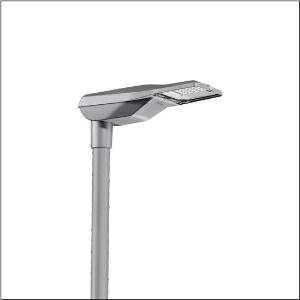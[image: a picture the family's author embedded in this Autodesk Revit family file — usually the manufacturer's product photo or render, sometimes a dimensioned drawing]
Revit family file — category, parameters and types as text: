
# Revit family: streetlight_sl_21_micro___st1_0a_5xe5d43a08db_2c1a
name_source: partatom
category: Lighting Fixtures
units: mm (PartAtom-declared; Revit-internal decimal feet)

## family parameters
Cut with Voids When Loaded = No
Host = Face
Light Source = No
Part Type = Normal
Room Calculation Point = No
Round Connector Dimension = Use Diameter
Shared = No

## types (1)
- --- (1 x LED, 5320 lm, 39.1 W, 4000K)
    Apparent Load = 39 VA
    CIE Flux Codes = 37 72 97 100 100
    Color Rendering = 70
    Color Temperature = 4000K
    Default Elevation = 1800 mm
    Description = Streetlight SL 21 micro, mast luminaire, primary light control with lens, of PMMA, primary optical cover: cover, of toughened safety glass, transparent, light distribution: ST1.0a, light emission: direct distribution, primary light characteristic: asymmetric, installation type: side-entry, post-top, LED, 3G 1.5mm², High Power LED, rated luminous flux: 5.320lm, luminous efficacy: 136lm/W, light colour: 740, colour temperature: 4000K, control: flexible luminous flux parameterisation, time-dependent luminous flux control, constant luminous flux control, overheat protection, mains connection: 230..240V, AC, 50/60Hz, connection cable pre-assembled, cable length: 6,5m, wiring characteristics: H07RN-F, start of lifetime: 39W, end of service life: 41W, reduction: 18W, luminaire housing, of diecast aluminium, powder-coated, Siteco® metallic grey (DB 702S), corrosivity category C5 mid according to DIN EN ISO 12944, please order mast flange separately, inclination adjustable: 0°, 5°, 10°, 15°, sealing non-destructively replaceable, multi-level sealing system, length: 528mm, width: 235mm, height: 110mm, mast flange for spigot size: 42mm (side-entry): 5XC10008XM4, 60/48mm (side-entry/post-top): 5XC10108XM2, 76/60mm (side-entry/post-top): 5XC10108XM1, protection rating (complete): IP66, insulation class (complete): insulation class II (safety insulation), certification: CE, ENEC, ENEC+, VDE, impact resistance: IK09, permissible operating ambient temperature for outdoor applications: -40..+50°C, standard-compliant lighting for roads and squares, packaging unit: 1 piece

Light Distribution: ST1.0a
    Height = 110 mm
    Lamp = 1 x LED
    Lamp Light Flux = 5320 lm
    Lamp Power = 39.1 W
    Lamp count = 1
    Length = 528 mm
    Luminous efficacy = 136 lm/W
    Manufacturer = Siteco
    ModVariant = No
    Model = 5XE5D43A08DB
    Number of Poles = 1
    OnlyDefault = Yes
    Power Factor = 1
    Product Name = Streetlight SL 21 micro | ST1.0a
    Product group = mast luminaire | pylon top
    ProductGroupID = 6100
    Protection Class = Protection class II
    Protection Degree = IP 66
    RLX_Detail_Level = 1
    RLX_Emergency_Light_Flux = 0 lm
    RLX_Emergency_Type = 0
    RLX_Emergency_Type_DB = No
    RlxData = <blob elided: 98429 chars, md5=3dc6498a>
    Socket = socket
    Standby Power = 0 W
    System Light Flux = 5320 lm
    System Power = 39 W
    Type Comments = factory setting: luminous flux: 100 % | Output Level: 100 % | 765 mA
    Type Image = l_1006881.jpg
    URL = http://relux.com
    VarID = @adj_105721
    Voltage = 0 V
    Weight = 0.00 kg
    Width = 235 mm

## geometry (parser evidence)
native form markers: Blend x4, Sweep x10
no freeform markers — native parametric forms only
